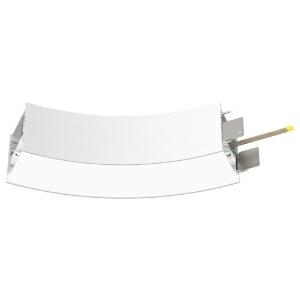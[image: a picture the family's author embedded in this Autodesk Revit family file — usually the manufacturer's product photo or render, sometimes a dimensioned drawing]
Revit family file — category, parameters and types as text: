
# Revit family: super-g_slim_super_g_slim_800_45deg_ab_ps_led__6w_790lm_3000k_cri_80_350-1340_4195
name_source: partatom
category: Leuchten
revit_build: Autodesk Revit 2016 (Build: 20190508_0715(x64)
units: mm (PartAtom-declared; Revit-internal decimal feet)

## family parameters
Basisbauteil = Fläche
Beim Laden mit Abzugskörper schneiden = Nein
Bemaßung runder Anschluss = Durchmesser verwenden
Gemeinsam genutzt = Nein
Lichtquelle = Nein
Raumberechnungspunkt = Nein
Teiletyp = Normal

## types (1)
- 350-1340-D01 (1 x LED, 480 lm, 3000K)
    Approval mark = CE
    Beschreibung = The insert consists of aluminum-extruded profile. Charming SOFT-EDGE design ensure unparalleled styling. The ballast is integrated and allows for an operation with 220-240V (50/60Hz). SUPER-G SLIM (# 350-1340) ist not dimmable (on/off).
    CIE Flux Codes = 48 79 96 100 71
    Color Rendering = 1B/80…89
    Color Temperature = 3000K
    Height = 90 mm
    Hersteller = Prolicht
    Lamp Light Flux = 480 lm
    Lamp count = 1
    Lampe = 1 x LED
    Length = 144 mm
    Luminous efficacy = 103 lm/W
    ModVariant = Nein
    Modell = 350-1340
    Mounting Place = Ceiling
    Mounting Type = Surface mounted
    Number of Poles = 1
    OnlyDefault = Ja
    Power Factor = 1
    Product Name = SUPER-G SLIM__SUPER G SLIM 800/45° AB PS LED: 6W 790lm 3000K CRI:80
    Product group = Surface profile systems
    ProductGroupID = 335
    Protection Class = Protection class I
    Protection Degree = IP 20
    RLX_Detail_Level = 1
    RlxData = <blob elided: 37613 chars, md5=3099b686>
    Scheinlast = 7 VA
    Socket = socket
    Standby Power = 0 W
    System Light Flux = 681 lm
    System Power = 7 W
    Typenbild = 350-1340.jpg
    URL = http://relux.com
    VarID = 350-1340-d01
    Voltage = 0 V
    Vorgabe-Ansicht = 1800 mm
    Weight = 0.00 kg
    Width = 65 mm

## geometry (parser evidence)
native form markers: Sweep x15
no freeform markers — native parametric forms only
